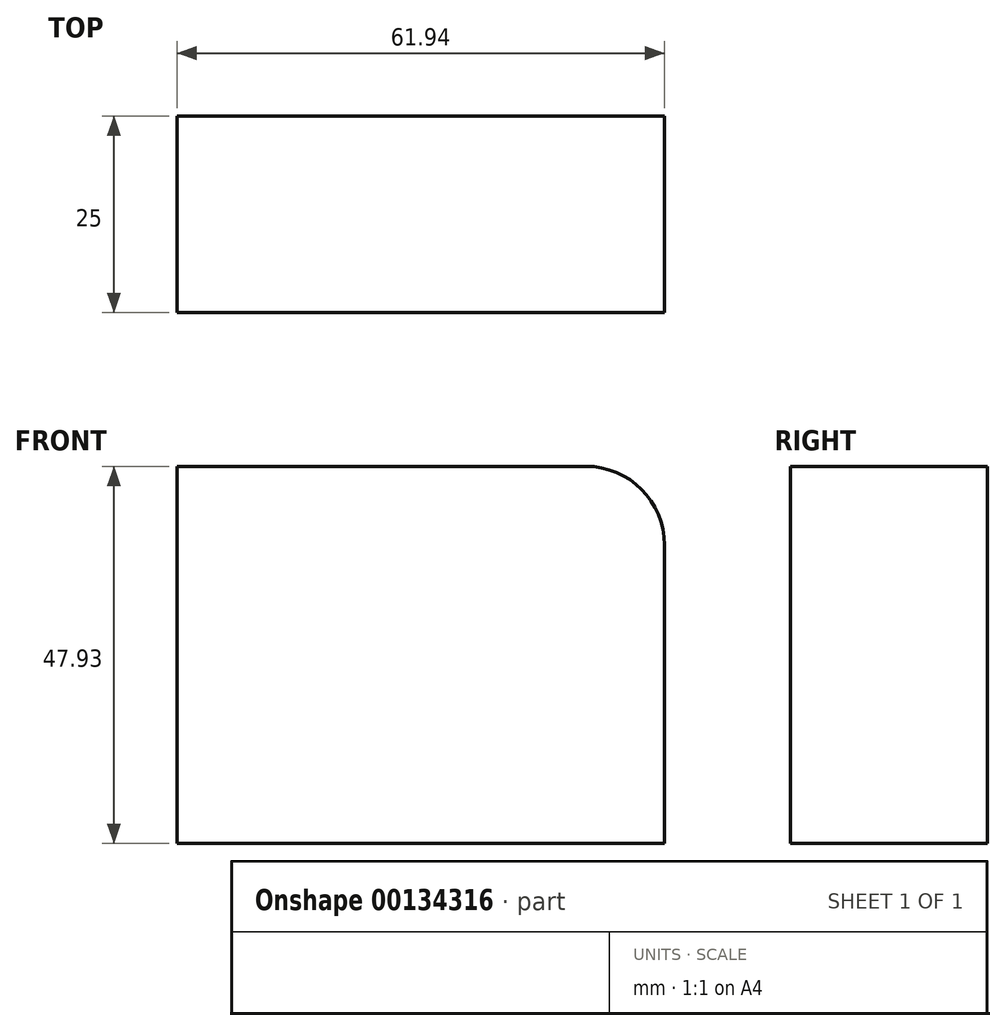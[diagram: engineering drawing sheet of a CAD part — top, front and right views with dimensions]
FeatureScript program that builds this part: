
annotation { "Feature Type Name" : "Feature", "Feature Type Description" : "" }
export const myFeature = defineFeature(function(context is Context, id is Id, definition is map)
    precondition{}
    {
        {
            var Q0;
            Q0=qCreatedBy(makeId("Front.planeOp"),FACE);
            var sketch = newSketch(context, id + "F0", { "sketchPlane" : qUnion([Q0])});
            skLineSegment(sketch, "E0.bottom", {"start": v(0, 0) * mm, "end": v(61.94, 0) * mm});
            skLineSegment(sketch, "E0.top", {"start": v(0, 47.93) * mm, "end": v(61.94, 47.93) * mm});
            skLineSegment(sketch, "E0.left", {"start": v(0, 0) * mm, "end": v(0, 47.93) * mm});
            skLineSegment(sketch, "E0.right", {"start": v(61.94, 0) * mm, "end": v(61.94, 47.93) * mm});
            skSolve(sketch);
        }
        {
            var Q0;
            Q0 = qSketchRegion(id + "F0", true);
            extrude(context, id + "F1", {"entities" : qUnion([Q0]), "depth" : 25 * mm});
        }
        {
            var Q0;
            Q0=makeQuery(id+"F1.opExtrude","SWEPT_EDGE",EDGE,{"disambiguationData":[OSD([sQuery(id+"F0.wireOp",EDGE,"E0.top"),sQuery(id+"F0.wireOp",EDGE,"E0.right")])]});
            fillet(context, id + "F2", {"entities" : qUnion([Q0]), "radius" : 10 * mm, "tangentPropagation" : true, "allowEdgeOverflow" : false});
        }
    });
